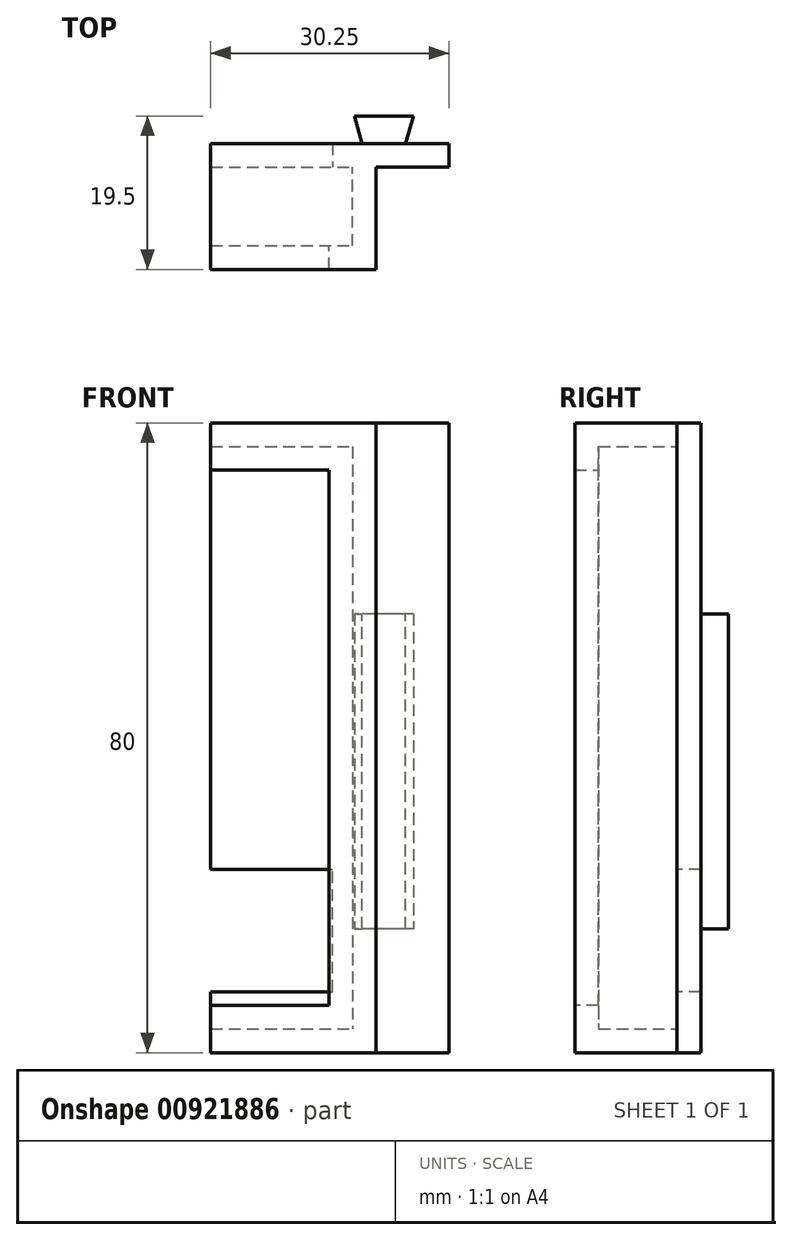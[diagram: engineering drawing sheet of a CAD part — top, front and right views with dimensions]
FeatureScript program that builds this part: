
annotation { "Feature Type Name" : "Feature", "Feature Type Description" : "" }
export const myFeature = defineFeature(function(context is Context, id is Id, definition is map)
    precondition{}
    {
        {
            var Q0;
            Q0=qCreatedBy(makeId("Front.planeOp"),FACE);
            var sketch = newSketch(context, id + "F0", { "sketchPlane" : qUnion([Q0])});
            skLineSegment(sketch, "E0.bottom", {"start": v(0, 0) * mm, "end": v(30.25, 0) * mm});
            skLineSegment(sketch, "E0.top", {"start": v(0, 80) * mm, "end": v(30.25, 80) * mm});
            skLineSegment(sketch, "E0.left", {"start": v(0, 0) * mm, "end": v(0, 80) * mm});
            skLineSegment(sketch, "E0.right", {"start": v(30.25, 0) * mm, "end": v(30.25, 80) * mm});
            skSolve(sketch);
        }
        {
            var Q0;
            Q0=makeQuery(id+"F0.imprint","IMPRINT",FACE,{"disambiguationData":[TD([[makeQuery(id+"F0.imprint","IMPRINT",EDGE,{"derivedFrom":sQuery(id+"F0.wireOp",EDGE,"E0.bottom")}),1.0]])]});
            extrude(context, id + "F1", {"entities" : qUnion([Q0]), "depth" : 3 * mm, "offsetDistance" : 25 * mm});
        }
        {
            var Q0;
            Q0=makeQuery(id+"F1.opExtrude","CAP_FACE",FACE,{"disambiguationData":[OSD([sQuery(id+"F0.wireOp",EDGE,"E0.bottom"),sQuery(id+"F0.wireOp",EDGE,"E0.top"),sQuery(id+"F0.wireOp",EDGE,"E0.left"),sQuery(id+"F0.wireOp",EDGE,"E0.right")])],"isStart":false});
            var sketch = newSketch(context, id + "F2", { "sketchPlane" : qUnion([Q0])});
            skLineSegment(sketch, "E1.bottom", {"start": v(0, 3) * mm, "end": v(18, 3) * mm});
            skLineSegment(sketch, "E1.top", {"start": v(0, 77) * mm, "end": v(18, 77) * mm});
            skLineSegment(sketch, "E1.left", {"start": v(0, 3) * mm, "end": v(0, 77) * mm});
            skLineSegment(sketch, "E1.right", {"start": v(18, 3) * mm, "end": v(18, 77) * mm});
            skLineSegment(sketch, "E2.bottom", {"start": v(0, 7.75) * mm, "end": v(15.5, 7.75) * mm});
            skLineSegment(sketch, "E2.top", {"start": v(0, 23.25) * mm, "end": v(15.5, 23.25) * mm});
            skLineSegment(sketch, "E2.left", {"start": v(0, 7.75) * mm, "end": v(0, 23.25) * mm});
            skLineSegment(sketch, "E2.right", {"start": v(15.5, 7.75) * mm, "end": v(15.5, 23.25) * mm});
            skLineSegment(sketch, "E3", {"start": v(21, 80) * mm, "end": v(21, 0) * mm});
            skSolve(sketch);
        }
        {
            var Q0;
            {var subQ0=sQuery(id+"F2.wireOp",EDGE,"E2.bottom");Q0=makeQuery(id+"F2.imprint","IMPRINT",FACE,{"disambiguationData":[TD([[makeQuery(id+"F2.imprint","IMPRINT",EDGE,{"derivedFrom":subQ0}),1.0]])]});}
            extrude(context, id + "F3", {"entities" : qUnion([Q0]), "operationType" : NewBodyOperationType.REMOVE, "oppositeDirection" : true, "depth" : 3 * mm, "offsetDistance" : 25 * mm});
        }
        {
            var Q0;
            {var subQ6=sQuery(id+"F2.wireOp",EDGE,"E1.bottom");Q0=makeQuery(id+"F2.imprint","IMPRINT",FACE,{"disambiguationData":[TD([[makeQuery(id+"F2.imprint","IMPRINT",EDGE,{"derivedFrom":subQ6}),-1.0]])]});}
            extrude(context, id + "F4", {"entities" : qUnion([Q0]), "operationType" : NewBodyOperationType.ADD, "depth" : 13 * mm, "offsetDistance" : 25 * mm});
        }
        {
            var Q0;
            Q0=makeQuery(id+"F4.opExtrude","SWEPT_FACE",FACE,{"disambiguationData":[OSD([sQuery(id+"F2.wireOp",EDGE,"E1.right")])]});
            var sketch = newSketch(context, id + "F5", { "sketchPlane" : qUnion([Q0])});
            skLineSegment(sketch, "E4.bottom", {"start": v(16, 3) * mm, "end": v(13, 3) * mm});
            skLineSegment(sketch, "E4.top", {"start": v(16, 77) * mm, "end": v(13, 77) * mm});
            skLineSegment(sketch, "E4.left", {"start": v(16, 3) * mm, "end": v(16, 77) * mm});
            skLineSegment(sketch, "E4.right", {"start": v(13, 3) * mm, "end": v(13, 77) * mm});
            skSolve(sketch);
        }
        {
            var Q0;
            Q0=makeQuery(id+"F4.opExtrude","SWEPT_FACE",FACE,{"disambiguationData":[OSD([sQuery(id+"F2.wireOp",EDGE,"E1.bottom")])]});
            var sketch = newSketch(context, id + "F6", { "sketchPlane" : qUnion([Q0])});
            skLineSegment(sketch, "E5.bottom", {"start": v(0, -16) * mm, "end": v(18, -16) * mm});
            skLineSegment(sketch, "E5.top", {"start": v(0, -13) * mm, "end": v(18, -13) * mm});
            skLineSegment(sketch, "E5.left", {"start": v(0, -16) * mm, "end": v(0, -13) * mm});
            skLineSegment(sketch, "E5.right", {"start": v(18, -16) * mm, "end": v(18, -13) * mm});
            skSolve(sketch);
        }
        {
            var Q0;
            Q0=makeQuery(id+"F6.imprint","IMPRINT",FACE,{"disambiguationData":[TD([[makeQuery(id+"F6.imprint","IMPRINT",EDGE,{"derivedFrom":sQuery(id+"F6.wireOp",EDGE,"E5.bottom")}),1.0]])]});
            extrude(context, id + "F7", {"entities" : qUnion([Q0]), "operationType" : NewBodyOperationType.ADD, "depth" : 3 * mm, "offsetDistance" : 25 * mm});
        }
        {
            var Q0;
            Q0=makeQuery(id+"F5.imprint","IMPRINT",FACE,{"disambiguationData":[TD([[makeQuery(id+"F5.imprint","IMPRINT",EDGE,{"derivedFrom":sQuery(id+"F5.wireOp",EDGE,"E4.bottom")}),-1.0]])]});
            extrude(context, id + "F8", {"entities" : qUnion([Q0]), "operationType" : NewBodyOperationType.ADD, "depth" : 3 * mm, "offsetDistance" : 25 * mm});
        }
        {
            var Q0;
            Q0=makeQuery(id+"F4.opExtrude","SWEPT_FACE",FACE,{"disambiguationData":[OSD([sQuery(id+"F2.wireOp",EDGE,"E1.top")])]});
            var sketch = newSketch(context, id + "F9", { "sketchPlane" : qUnion([Q0])});
            skLineSegment(sketch, "E6.bottom", {"start": v(0, 16) * mm, "end": v(15, 16) * mm});
            skLineSegment(sketch, "E6.top", {"start": v(0, 13) * mm, "end": v(15, 13) * mm});
            skLineSegment(sketch, "E6.left", {"start": v(0, 16) * mm, "end": v(0, 13) * mm});
            skLineSegment(sketch, "E6.right", {"start": v(15, 16) * mm, "end": v(15, 13) * mm});
            skSolve(sketch);
        }
        {
            var Q0;
            Q0=makeQuery(id+"F9.imprint","IMPRINT",FACE,{"disambiguationData":[TD([[makeQuery(id+"F9.imprint","IMPRINT",EDGE,{"derivedFrom":sQuery(id+"F9.wireOp",EDGE,"E6.bottom")}),-1.0]])]});
            extrude(context, id + "F10", {"entities" : qUnion([Q0]), "operationType" : NewBodyOperationType.ADD, "depth" : 3 * mm, "offsetDistance" : 25 * mm});
        }
        {
            var Q0;
            Q0=makeQuery(id+"F1.opExtrude","CAP_FACE",FACE,{"disambiguationData":[OSD([sQuery(id+"F0.wireOp",EDGE,"E0.bottom"),sQuery(id+"F0.wireOp",EDGE,"E0.top"),sQuery(id+"F0.wireOp",EDGE,"E0.left"),sQuery(id+"F0.wireOp",EDGE,"E0.right")])],"isStart":true});
            var sketch = newSketch(context, id + "F11", { "sketchPlane" : qUnion([Q0])});
            skLineSegment(sketch, "E7.bottom", {"start": v(-25.75, 80) * mm, "end": v(-18.25, 80) * mm});
            skLineSegment(sketch, "E7.top", {"start": v(-25.75, 15.75) * mm, "end": v(-18.25, 15.75) * mm});
            skLineSegment(sketch, "E7.left", {"start": v(-25.75, 80) * mm, "end": v(-25.75, 15.75) * mm});
            skLineSegment(sketch, "E7.right", {"start": v(-18.25, 80) * mm, "end": v(-18.25, 15.75) * mm});
            skLineSegment(sketch, "E8", {"start": v(-25.75, 55.75) * mm, "end": v(-18.25, 55.75) * mm});
            skSolve(sketch);
        }
        {
            var Q0;
            {var subQ0=sQuery(id+"F11.wireOp",EDGE,"E7.top");Q0=makeQuery(id+"F11.imprint","IMPRINT",FACE,{"disambiguationData":[TD([[makeQuery(id+"F11.imprint","IMPRINT",EDGE,{"derivedFrom":subQ0}),1.0]])]});}
            extrude(context, id + "F12", {"entities" : qUnion([Q0]), "operationType" : NewBodyOperationType.ADD, "depth" : 3.5 * mm, "offsetDistance" : 25 * mm});
        }
        {
            var Q0;
            Q0=makeQuery(id+"F12.opExtrude","SWEPT_FACE",FACE,{"disambiguationData":[OSD([sQuery(id+"F11.wireOp",EDGE,"E8")])]});
            var sketch = newSketch(context, id + "F13", { "sketchPlane" : qUnion([Q0])});
            skLineSegment(sketch, "E9", {"start": v(25.75, 3.5) * mm, "end": v(24.75, 0) * mm});
            skLineSegment(sketch, "E10", {"start": v(24.75, 0) * mm, "end": v(25.75, 0) * mm});
            skLineSegment(sketch, "E11", {"start": v(18.25, 3.5) * mm, "end": v(19.25, 0) * mm});
            skLineSegment(sketch, "E12", {"start": v(19.25, 0) * mm, "end": v(18.25, 0) * mm});
            skSolve(sketch);
        }
        {
            var Q0;
            Q0=makeQuery(id+"F13.imprint","IMPRINT",FACE,{"disambiguationData":[TD([[makeQuery(id+"F13.imprint","IMPRINT",EDGE,{"derivedFrom":sQuery(id+"F13.wireOp",EDGE,"E9")}),1.0]])]});
            var Q1;
            Q1=makeQuery(id+"F13.imprint","IMPRINT",FACE,{"disambiguationData":[TD([[makeQuery(id+"F13.imprint","IMPRINT",EDGE,{"derivedFrom":sQuery(id+"F13.wireOp",EDGE,"E11")}),-1.0]])]});
            extrude(context, id + "F14", {"entities" : qUnion([Q0, Q1]), "operationType" : NewBodyOperationType.REMOVE, "oppositeDirection" : true, "depth" : 40 * mm, "offsetDistance" : 25 * mm});
        }
    });
